# Revit family: Guard 100E
name_source: partatom
category: Wyposażenie mechaniczne
revit_build: Autodesk Revit 2018 (Build: 20170927_1515(x64)
units: mm (PartAtom-declared; Revit-internal decimal feet)

## family parameters
Klasyfikacja = Brak
Obiekt nadrzędny = Powierzchnia
Punkt obliczania pomieszczeń = Nie
Tnij formami wycięć po wczytaniu = Nie
Typ części = Normalny
Współdzielony = Nie
Wymiar okrągłego złącza = Użyj średnicy

## types (1)
- Guard 100E
    Autor = www.archispace.com
    Domyślna rzędna = 1500 mm
    Model = Guard 100E
    Opis = Воздушно-тепловая завеса
    Producent = Sonninger Sp. z o.o. Sp. k.
    Диаметры патрубков = 12.7
    Длина завесы = 1 mm  [stored 0.00328084 ft]
    Класс защиты = IP21
    Максимальная высота двери = 4 mm  [stored 0.0131234 ft]
    Максимальный расход воздуха = 2000.0 m³/h
    Масса оборудования = 17.00 kg
    Мощность обогрева max. = 7 kW
    Мощность обогрева min. = 4 kW
    Мощность электродвигателя = 220 W
    Напряжение питания = 230 V
    Напряжение питания нагревателя = 400 V
    Потребление тока = 11 A
    Уровень шума = 59
    двигатель потребление тока = 2 A
    конец растяжения = 531 mm  [stored 1.74213 ft]
    материал = Body - PPT material+metal RAL2006
    начало растяжения = -531 mm
    нижний материал = Ral 9011

note: [stored X ft] marks values corroborated as IEEE doubles in the binary element streams (Revit-internal decimal feet)
